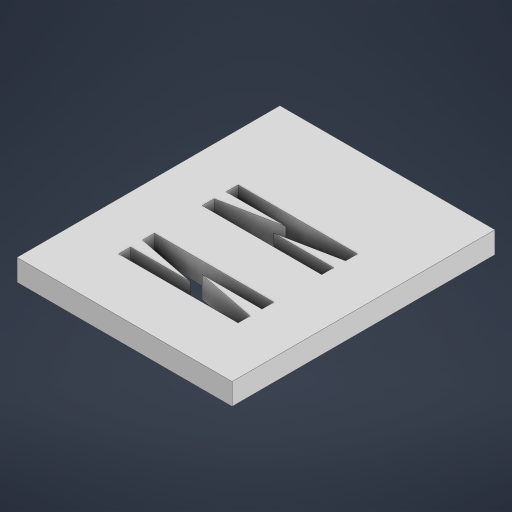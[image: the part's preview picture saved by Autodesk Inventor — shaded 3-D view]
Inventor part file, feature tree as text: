
AUTODESK INVENTOR PART (.ipt)
format: ipt  version: 2024 (Build 280153000, 153)  size: 195,584 bytes
history: native  units: mm
features: other x1, extrude x1, sketch x1
ambient origin geometry x8: Origin, YZ Plane, XZ Plane, XY Plane, X Axis, Y Axis, Z Axis, Center Point
bodies: Body1 (feature_tree)
feature tree (3):
  other  "Sólido1"
  extrude  "Extrusión1"  Depth=220.0mm
  sketch  "Boceto1"  dims[d0=180.0mm d1=220.0mm d2=90.0mm d3=0.0mm d5=10.0mm d6=40.0mm d7=10.0mm d8=10.0mm d9=100.0mm d11=45.0mm d13=10.0mm d14=10.0mm d15=10.0mm d16=75.0mm d17=18.0mm d18=0.0mm]
